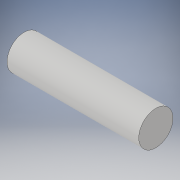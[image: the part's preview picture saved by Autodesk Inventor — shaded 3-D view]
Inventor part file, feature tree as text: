
AUTODESK INVENTOR PART (.ipt)
format: ipt  version: 2019 (Build 230136000, 136)  size: 92,160 bytes
history: native  units: in
note: dims shown in document units (in); Inventor stores cm internally (conversion verified against a paired STEP export)
features: revolve x1, sketch x1
ambient origin geometry x8: Origin, YZ Plane, XZ Plane, XY Plane, X Axis, Y Axis, Z Axis, Center Point
bodies: Solid1 (feature_tree)
feature tree (2):
  revolve  "Revolution1"  [1 undecoded]
  sketch  "Sketch1"  dims[d0=0.5118in d1=3.937in d2=90.0deg]
note: 1 required parameter value undecoded (feature->parameter linkage not recoverable at this tier; creation-order binding heuristic only, values carry confidence <= 0.55)
